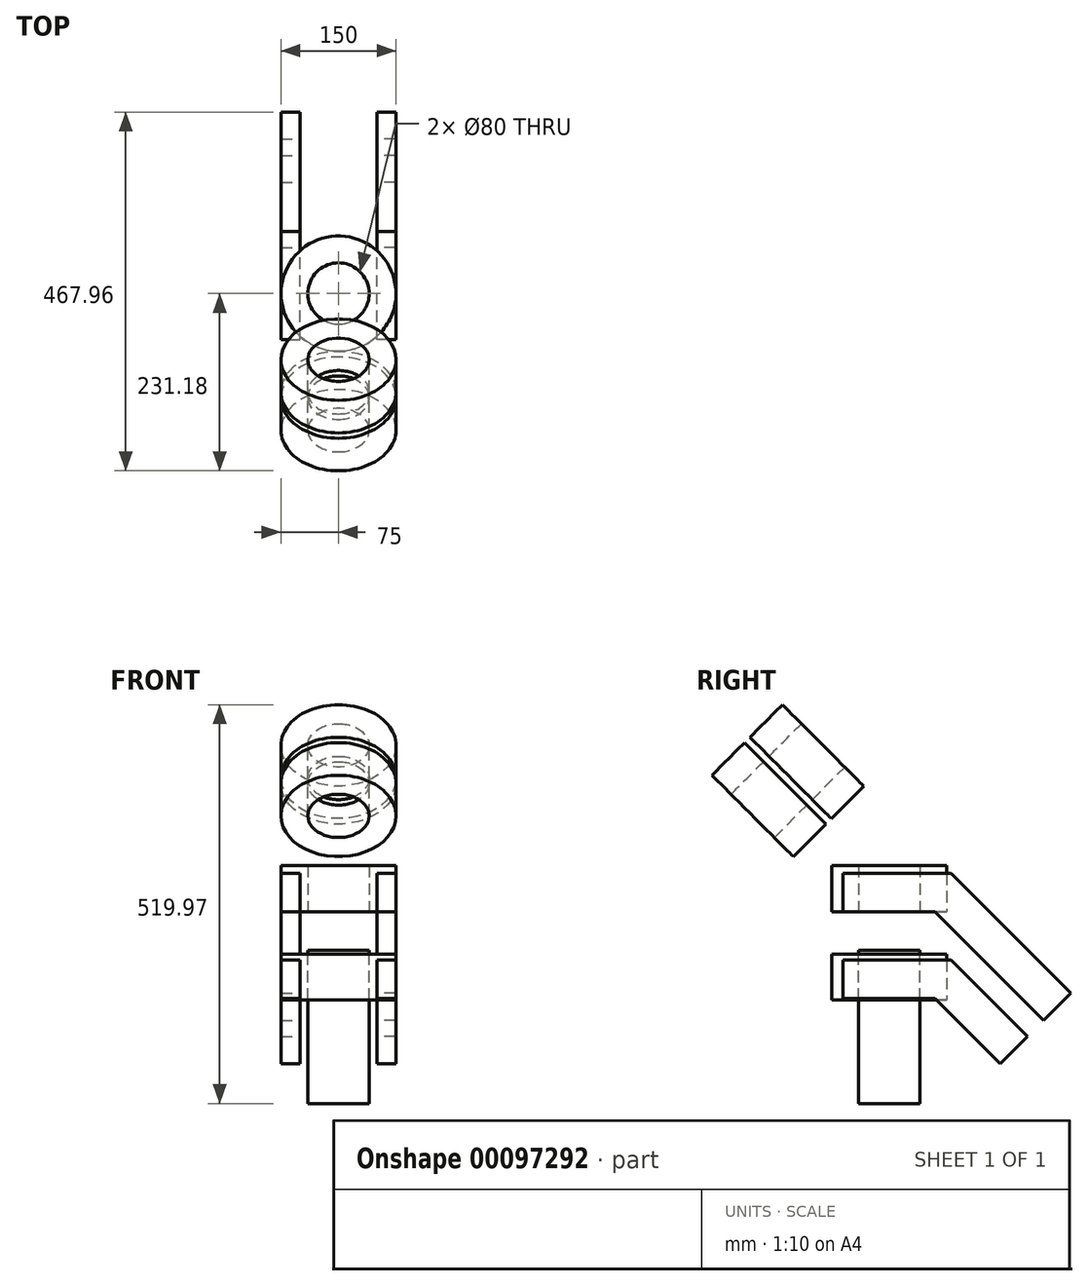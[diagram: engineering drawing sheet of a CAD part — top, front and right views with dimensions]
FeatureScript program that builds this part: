
annotation { "Feature Type Name" : "Feature", "Feature Type Description" : "" }
export const myFeature = defineFeature(function(context is Context, id is Id, definition is map)
    precondition{}
    {
        {
            var Q0;
            Q0=qCreatedBy(makeId("Right.planeOp"),FACE);
            var sketch = newSketch(context, id + "F0", { "sketchPlane" : qUnion([Q0])});
            skLineSegment(sketch, "E0.bottom", {"start": v(-60, -25) * mm, "end": v(60, -25) * mm});
            skLineSegment(sketch, "E0.top", {"start": v(-60, 25) * mm, "end": v(60, 25) * mm});
            skLineSegment(sketch, "E0.left", {"start": v(-60, -25) * mm, "end": v(-60, 25) * mm});
            skPoint(sketch, "E0.middle", {"position": v(0, 0) * mm});
            skLineSegment(sketch, "E1", {"start": v(60, -25) * mm, "end": v(201.42, -166.42) * mm});
            skLineSegment(sketch, "E2", {"start": v(236.78, -131.07) * mm, "end": v(95.36, 10.36) * mm});
            skLineSegment(sketch, "E3", {"start": v(60, -25) * mm, "end": v(95.36, 10.36) * mm});
            skLineSegment(sketch, "E4", {"start": v(60, -25) * mm, "end": v(60, 25) * mm});
            skLineSegment(sketch, "E5.bottom", {"start": v(-40, -272.23) * mm, "end": v(40, -272.23) * mm});
            skLineSegment(sketch, "E5.top", {"start": v(-40, -72.23) * mm, "end": v(40, -72.23) * mm});
            skLineSegment(sketch, "E5.left", {"start": v(-40, -272.23) * mm, "end": v(-40, -72.23) * mm});
            skLineSegment(sketch, "E5.right", {"start": v(40, -272.23) * mm, "end": v(40, -72.23) * mm});
            skPoint(sketch, "E5.middle", {"position": v(0, -172.23) * mm});
            skLineSegment(sketch, "E6", {"start": v(95.36, -102.78) * mm, "end": v(180.2, -187.63) * mm});
            skLineSegment(sketch, "E7", {"start": v(144.85, -222.99) * mm, "end": v(60, -138.14) * mm});
            skLineSegment(sketch, "E8", {"start": v(95.36, -102.78) * mm, "end": v(60, -138.14) * mm});
            skLineSegment(sketch, "E9.bottom", {"start": v(-60, -138.14) * mm, "end": v(60, -138.14) * mm});
            skLineSegment(sketch, "E9.top", {"start": v(-60, -88.14) * mm, "end": v(60, -88.14) * mm});
            skLineSegment(sketch, "E9.left", {"start": v(-60, -138.14) * mm, "end": v(-60, -88.14) * mm});
            skLineSegment(sketch, "E9.right", {"start": v(60, -138.14) * mm, "end": v(60, -88.14) * mm});
            skPoint(sketch, "E9.middle", {"position": v(0, -113.14) * mm});
            skLineSegment(sketch, "E10", {"start": v(144.85, -222.99) * mm, "end": v(236.78, -131.07) * mm});
            skLineSegment(sketch, "E11", {"start": v(60, 25) * mm, "end": v(80.71, 25) * mm});
            skLineSegment(sketch, "E12", {"start": v(95.36, 10.36) * mm, "end": v(80.71, 25) * mm});
            skLineSegment(sketch, "E13", {"start": v(60, -88.14) * mm, "end": v(80.71, -88.14) * mm});
            skLineSegment(sketch, "E14", {"start": v(95.36, -102.78) * mm, "end": v(80.71, -88.14) * mm});
            skSolve(sketch);
        }
        {
            var Q0;
            {var subQ0=sQuery(id+"F0.wireOp",EDGE,"E1");Q0=makeQuery(id+"F0.imprint","IMPRINT",FACE,{"disambiguationData":[TD([[makeQuery(id+"F0.imprint","IMPRINT",EDGE,{"derivedFrom":subQ0}),1.0]])]});}
            var Q1;
            Q1=makeQuery(id+"F0.imprint","IMPRINT",FACE,{"disambiguationData":[TD([[makeQuery(id+"F0.imprint","IMPRINT",EDGE,{"derivedFrom":sQuery(id+"F0.wireOp",EDGE,"E3")}),1.0]])]});
            var Q2;
            Q2=makeQuery(id+"F0.imprint","IMPRINT",FACE,{"disambiguationData":[TD([[makeQuery(id+"F0.imprint","IMPRINT",EDGE,{"derivedFrom":sQuery(id+"F0.wireOp",EDGE,"E0.bottom")}),1.0]])]});
            var Q3;
            {var subQ0=sQuery(id+"F0.wireOp",EDGE,"E6");Q3=makeQuery(id+"F0.imprint","IMPRINT",FACE,{"disambiguationData":[TD([[makeQuery(id+"F0.imprint","IMPRINT",EDGE,{"derivedFrom":subQ0}),-1.0]])]});}
            var Q4;
            Q4=makeQuery(id+"F0.imprint","IMPRINT",FACE,{"disambiguationData":[TD([[makeQuery(id+"F0.imprint","IMPRINT",EDGE,{"derivedFrom":sQuery(id+"F0.wireOp",EDGE,"E8")}),-1.0]])]});
            var Q5;
            {var subQ5=sQuery(id+"F0.wireOp",EDGE,"E9.right");Q5=makeQuery(id+"F0.imprint","IMPRINT",FACE,{"disambiguationData":[TD([[makeQuery(id+"F0.imprint","IMPRINT",EDGE,{"derivedFrom":subQ5}),1.0]])]});}
            var Q6;
            {var subQ0=sQuery(id+"F0.wireOp",EDGE,"E9.bottom");var subQ1=sQuery(id+"F0.wireOp",EDGE,"E5.left");var subQ2=makeQuery(id+"F0.imprint","INTERSECT",VERTEX,{"derivedFrom":[subQ1,subQ0]});Q6=makeQuery(id+"F0.imprint","IMPRINT",FACE,{"disambiguationData":[TD([[makeQuery(id+"F0.imprint","IMPRINT",EDGE,{"disambiguationData":[TD([[subQ2,-1.0]])],"derivedFrom":subQ1}),-1.0]])]});}
            var Q7;
            {var subQ5=sQuery(id+"F0.wireOp",EDGE,"E9.left");Q7=makeQuery(id+"F0.imprint","IMPRINT",FACE,{"disambiguationData":[TD([[makeQuery(id+"F0.imprint","IMPRINT",EDGE,{"derivedFrom":subQ5}),-1.0]])]});}
            extrude(context, id + "F1", {"entities" : qUnion([Q0, Q1, Q2, Q3, Q4, Q5, Q6, Q7]), "depth" : 25 * mm});
        }
        {
            var Q0;
            Q0=makeQuery(id+"F1.opExtrude","SWEPT_BODY",BODY,{"disambiguationData":[OSD([sQuery(id+"F0.wireOp",EDGE,"E6"),sQuery(id+"F0.wireOp",EDGE,"E7"),sQuery(id+"F0.wireOp",EDGE,"E9.bottom"),sQuery(id+"F0.wireOp",EDGE,"E9.top"),sQuery(id+"F0.wireOp",EDGE,"E9.left"),sQuery(id+"F0.wireOp",EDGE,"E10"),sQuery(id+"F0.wireOp",EDGE,"b84716b3-d0dc-4534-8042-1133830b8f0b")])]});
            var Q1;
            Q1=makeQuery(id+"F1.opExtrude","SWEPT_BODY",BODY,{"disambiguationData":[OSD([sQuery(id+"F0.wireOp",EDGE,"E0.bottom"),sQuery(id+"F0.wireOp",EDGE,"E0.top"),sQuery(id+"F0.wireOp",EDGE,"E0.left"),sQuery(id+"F0.wireOp",EDGE,"E1"),sQuery(id+"F0.wireOp",EDGE,"E2"),sQuery(id+"F0.wireOp",EDGE,"947238e5-580d-4665-a6cb-fdf0ff862519"),sQuery(id+"F0.wireOp",EDGE,"E10")])]});
            transform(context, id + "F2", {"entities" : qUnion([Q0, Q1]), "transformType" : TransformType.TRANSLATION_3D, "dx" : 50 * mm, "dy" : 0 * mm, "dz" : 0 * mm, "makeCopy" : false});
        }
        {
            var Q0;
            Q0=makeQuery(id+"F1.opExtrude","SWEPT_BODY",BODY,{"disambiguationData":[OSD([sQuery(id+"F0.wireOp",EDGE,"E6"),sQuery(id+"F0.wireOp",EDGE,"E7"),sQuery(id+"F0.wireOp",EDGE,"E9.bottom"),sQuery(id+"F0.wireOp",EDGE,"E9.top"),sQuery(id+"F0.wireOp",EDGE,"E9.left"),sQuery(id+"F0.wireOp",EDGE,"E10"),sQuery(id+"F0.wireOp",EDGE,"b84716b3-d0dc-4534-8042-1133830b8f0b")])]});
            var Q1;
            Q1=makeQuery(id+"F1.opExtrude","SWEPT_BODY",BODY,{"disambiguationData":[OSD([sQuery(id+"F0.wireOp",EDGE,"E0.bottom"),sQuery(id+"F0.wireOp",EDGE,"E0.top"),sQuery(id+"F0.wireOp",EDGE,"E0.left"),sQuery(id+"F0.wireOp",EDGE,"E1"),sQuery(id+"F0.wireOp",EDGE,"E2"),sQuery(id+"F0.wireOp",EDGE,"947238e5-580d-4665-a6cb-fdf0ff862519"),sQuery(id+"F0.wireOp",EDGE,"E10")])]});
            var Q2;
            Q2=qCreatedBy(makeId("Right.planeOp"),FACE);
            mirror(context, id + "F3", {"entities" : qUnion([Q0, Q1]), "mirrorPlane" : qUnion([Q2])});
        }
        {
            var Q0;
            Q0=qCreatedBy(makeId("Top.planeOp"),FACE);
            var sketch = newSketch(context, id + "F4", { "sketchPlane" : qUnion([Q0])});
            skCircle(sketch, "E15", {"center": v(0, 0) * mm, "radius": 40 * mm});
            skCircle(sketch, "E16", {"center": v(0, 0) * mm, "radius": 50 * mm});
            skCircle(sketch, "E17", {"center": v(0, 0) * mm, "radius": 75 * mm});
            skSolve(sketch);
        }
        {
            var Q0;
            Q0=makeQuery(id+"F4.imprint","IMPRINT",FACE,{"disambiguationData":[TD([[makeQuery(id+"F4.imprint","IMPRINT",EDGE,{"derivedFrom":sQuery(id+"F4.wireOp",EDGE,"E15")}),1.0]])]});
            extrude(context, id + "F5", {"entities" : qUnion([Q0]), "oppositeDirection" : true, "depth" : 200 * mm});
        }
        {
            var Q0;
            Q0=makeQuery(id+"F5.opExtrude","SWEPT_BODY",BODY,{"disambiguationData":[OSD([sQuery(id+"F4.wireOp",EDGE,"E15")])]});
            transform(context, id + "F6", {"entities" : qUnion([Q0]), "transformType" : TransformType.TRANSLATION_3D, "dx" : 0 * mm, "dy" : 0 * mm, "dz" : -75 * mm, "makeCopy" : false});
        }
        {
            var Q0;
            Q0=makeQuery(id+"F4.imprint","IMPRINT",FACE,{"disambiguationData":[TD([[makeQuery(id+"F4.imprint","IMPRINT",EDGE,{"derivedFrom":sQuery(id+"F4.wireOp",EDGE,"E16")}),-1.0]])]});
            var Q1;
            Q1=makeQuery(id+"F4.imprint","IMPRINT",FACE,{"disambiguationData":[TD([[makeQuery(id+"F4.imprint","IMPRINT",EDGE,{"derivedFrom":sQuery(id+"F4.wireOp",EDGE,"E15")}),-1.0]])]});
            extrude(context, id + "F7", {"entities" : qUnion([Q0, Q1]), "depth" : 35 * mm, "hasSecondDirection" : true, "secondDirectionOppositeDirection" : true, "secondDirectionDepth" : 25 * mm});
        }
        {
            var Q0;
            Q0=makeQuery(id+"F1.opExtrude","SWEPT_FACE",FACE,{"disambiguationData":[OSD([sQuery(id+"F0.wireOp",EDGE,"E2"),sQuery(id+"F0.wireOp",EDGE,"E12")])]});
            var sketch = newSketch(context, id + "F8", { "sketchPlane" : qUnion([Q0])});
            skCircle(sketch, "E18", {"center": v(0, 196.7) * mm, "radius": 75 * mm});
            skCircle(sketch, "E19", {"center": v(0, 196.7) * mm, "radius": 40 * mm});
            skSolve(sketch);
        }
        {
            var Q0;
            Q0 = qSketchRegion(id + "F8", true);
            extrude(context, id + "F9", {"entities" : qUnion([Q0]), "oppositeDirection" : true, "depth" : 60 * mm});
        }
        {
            var Q0;
            Q0=makeQuery(id+"F9.opExtrude","SWEPT_BODY",BODY,{"disambiguationData":[OSD([sQuery(id+"F8.wireOp",EDGE,"E18"),sQuery(id+"F8.wireOp",EDGE,"E19")])]});
            var Q1;
            {var subQ0=sQuery(id+"F0.wireOp",EDGE,"E10");Q1=makeQuery(id+"F1.opExtrude","CAP_EDGE",EDGE,{"disambiguationData":[OSD([subQ0]),TDD([makeQuery(id+"F0.imprint","IMPRINT",EDGE,{"disambiguationData":[TD([[makeQuery(id+"F0.imprint","INTERSECT",VERTEX,{"derivedFrom":[sQuery(id+"F0.wireOp",EDGE,"E1"),subQ0]}),-1.0]])],"derivedFrom":subQ0})])],"isStart":false});}
            transform(context, id + "F10", {"entities" : qUnion([Q0]), "transformType" : TransformType.TRANSLATION_DISTANCE, "transformDirection" : qUnion([Q1]), "distance" : 70 * mm, "oppositeDirection" : true, "makeCopy" : true});
        }
        {
            var Q0;
            Q0=makeQuery(id+"F4.imprint","IMPRINT",FACE,{"disambiguationData":[TD([[makeQuery(id+"F4.imprint","IMPRINT",EDGE,{"derivedFrom":sQuery(id+"F4.wireOp",EDGE,"E15")}),-1.0]])]});
            var Q1;
            Q1=makeQuery(id+"F4.imprint","IMPRINT",FACE,{"disambiguationData":[TD([[makeQuery(id+"F4.imprint","IMPRINT",EDGE,{"derivedFrom":sQuery(id+"F4.wireOp",EDGE,"E16")}),-1.0]])]});
            extrude(context, id + "F11", {"entities" : qUnion([Q0, Q1]), "depth" : 60 * mm});
        }
        {
            var Q0;
            Q0=makeQuery(id+"F11.opExtrude","SWEPT_BODY",BODY,{"disambiguationData":[OSD([sQuery(id+"F4.wireOp",EDGE,"E15"),sQuery(id+"F4.wireOp",EDGE,"E17")])]});
            transform(context, id + "F12", {"entities" : qUnion([Q0]), "transformType" : TransformType.TRANSLATION_3D, "dx" : 0 * mm, "dy" : 0 * mm, "dz" : -140 * mm, "makeCopy" : false});
        }
    });
